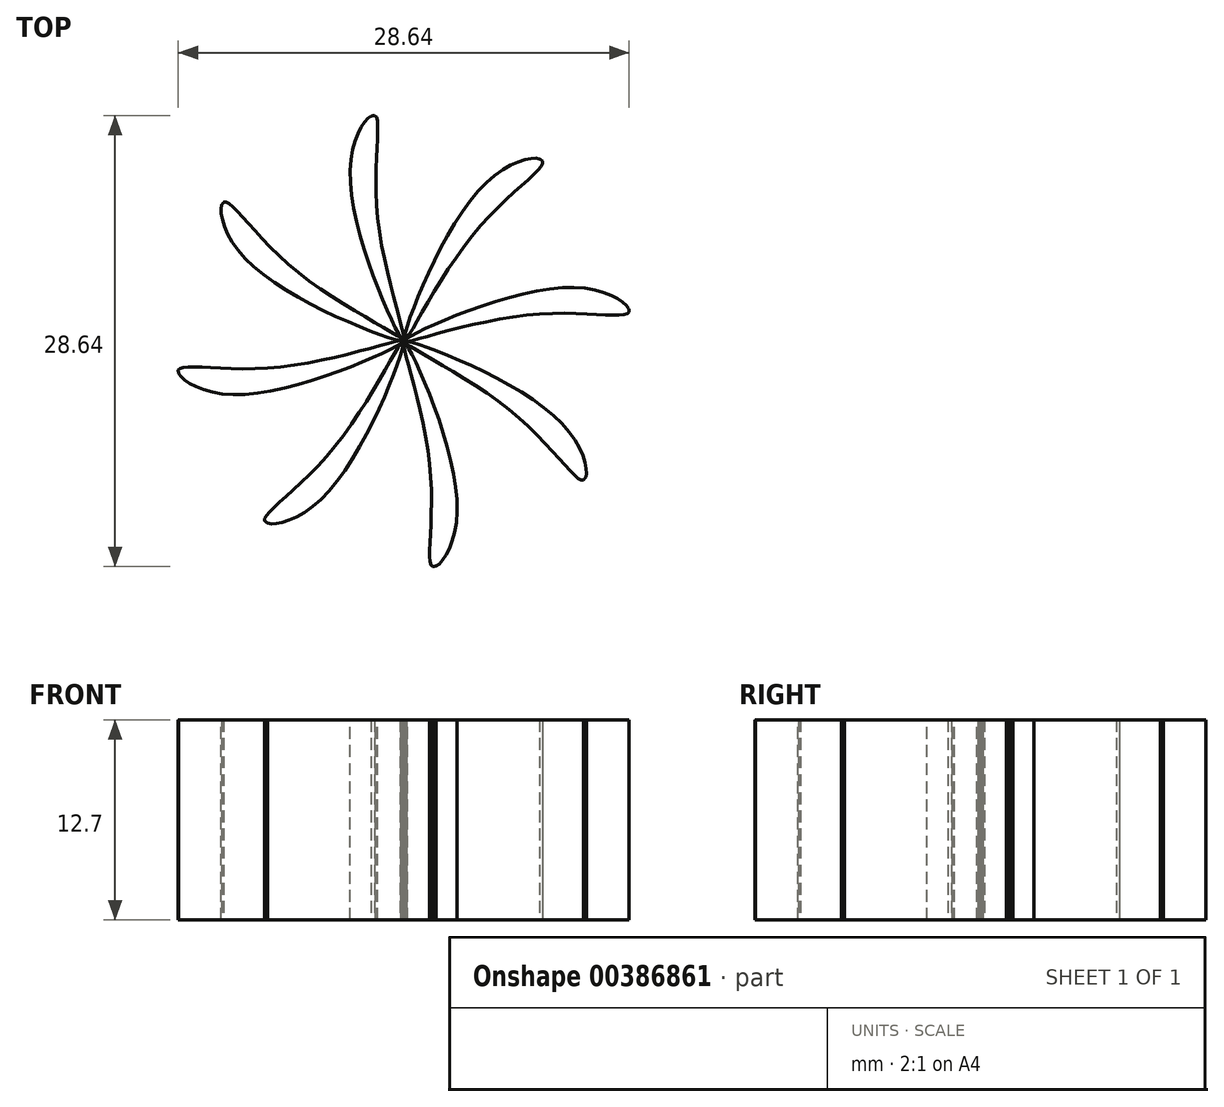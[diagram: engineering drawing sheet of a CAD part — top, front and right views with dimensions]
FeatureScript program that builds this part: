
annotation { "Feature Type Name" : "Feature", "Feature Type Description" : "" }
export const myFeature = defineFeature(function(context is Context, id is Id, definition is map)
    precondition{}
    {
        {
            var Q0;
            Q0=qCreatedBy(makeId("Top.planeOp"),FACE);
            var sketch = newSketch(context, id + "F0", { "sketchPlane" : qUnion([Q0])});
            skCircle(sketch, "E0", {"center": v(0, 0) * mm, "radius": 14.44 * mm});
            skFitSpline(sketch, "E1", {"points": [v(0, 0) * mm, v(-3.4, 10.76) * mm, v(-1.84, 14.32) * mm, v(-1.68, 8.08) * mm, v(0, 0) * mm]});
            skFitSpline(sketch, "E2", {"points": [v(0, 0) * mm, v(5.2, 10.02) * mm, v(8.83, 11.43) * mm, v(4.53, 6.9) * mm, v(0, 0) * mm]});
            skFitSpline(sketch, "E3", {"points": [v(0, 0) * mm, v(10.76, 3.4) * mm, v(14.32, 1.84) * mm, v(8.08, 1.68) * mm, v(0, 0) * mm]});
            skFitSpline(sketch, "E4", {"points": [v(0, 0) * mm, v(10.02, -5.2) * mm, v(11.43, -8.83) * mm, v(6.9, -4.53) * mm, v(0, 0) * mm]});
            skFitSpline(sketch, "E5", {"points": [v(0, 0) * mm, v(-10.02, 5.2) * mm, v(-11.43, 8.83) * mm, v(-6.9, 4.53) * mm, v(0, 0) * mm]});
            skFitSpline(sketch, "E6", {"points": [v(0, 0) * mm, v(-10.76, -3.4) * mm, v(-14.32, -1.84) * mm, v(-8.08, -1.68) * mm, v(0, 0) * mm]});
            skFitSpline(sketch, "E7", {"points": [v(0, 0) * mm, v(-5.2, -10.02) * mm, v(-8.83, -11.43) * mm, v(-4.53, -6.9) * mm, v(0, 0) * mm]});
            skFitSpline(sketch, "E8", {"points": [v(0, 0) * mm, v(3.4, -10.76) * mm, v(1.84, -14.32) * mm, v(1.68, -8.08) * mm, v(0, 0) * mm]});
            skSolve(sketch);
        }
        {
            var Q0;
            {var subQ0=sQuery(id+"F0.wireOp",EDGE,"E5");var subQ1=sQuery(id+"F0.wireOp",EDGE,"E0");var subQ2=makeQuery(id+"F0.imprint","INTERSECT",VERTEX,{"disambiguationData":[OD(0.0)],"derivedFrom":[subQ1,subQ0]});Q0=makeQuery(id+"F0.imprint","IMPRINT",FACE,{"disambiguationData":[TD([[makeQuery(id+"F0.imprint","IMPRINT",EDGE,{"disambiguationData":[TD([[subQ2,-1.0]])],"derivedFrom":subQ1}),1.0]])]});}
            var Q1;
            {var subQ1=sQuery(id+"F0.wireOp",EDGE,"E1");var subQ5=sQuery(id+"F0.wireOp",EDGE,"E0");var subQ6=makeQuery(id+"F0.imprint","INTERSECT",VERTEX,{"disambiguationData":[OD(0.0)],"derivedFrom":[subQ5,subQ1]});Q1=makeQuery(id+"F0.imprint","IMPRINT",FACE,{"disambiguationData":[TD([[makeQuery(id+"F0.imprint","IMPRINT",EDGE,{"disambiguationData":[TD([[subQ6,-1.0]])],"derivedFrom":subQ5}),1.0]])]});}
            var Q2;
            {var subQ0=sQuery(id+"F0.wireOp",EDGE,"E2");var subQ1=sQuery(id+"F0.wireOp",EDGE,"E0");var subQ2=makeQuery(id+"F0.imprint","INTERSECT",VERTEX,{"disambiguationData":[OD(0.0)],"derivedFrom":[subQ1,subQ0]});Q2=makeQuery(id+"F0.imprint","IMPRINT",FACE,{"disambiguationData":[TD([[makeQuery(id+"F0.imprint","IMPRINT",EDGE,{"disambiguationData":[TD([[subQ2,-1.0]])],"derivedFrom":subQ1}),1.0]])]});}
            var Q3;
            {var subQ0=sQuery(id+"F0.wireOp",EDGE,"E3");var subQ1=sQuery(id+"F0.wireOp",EDGE,"E0");var subQ5=makeQuery(id+"F0.imprint","INTERSECT",VERTEX,{"disambiguationData":[OD(0.0)],"derivedFrom":[subQ1,subQ0]});Q3=makeQuery(id+"F0.imprint","IMPRINT",FACE,{"disambiguationData":[TD([[makeQuery(id+"F0.imprint","IMPRINT",EDGE,{"disambiguationData":[TD([[subQ5,1.0]])],"derivedFrom":subQ1}),1.0]])]});}
            var Q4;
            {var subQ0=sQuery(id+"F0.wireOp",EDGE,"E4");var subQ1=sQuery(id+"F0.wireOp",EDGE,"E0");var subQ2=makeQuery(id+"F0.imprint","INTERSECT",VERTEX,{"disambiguationData":[OD(0.0)],"derivedFrom":[subQ1,subQ0]});Q4=makeQuery(id+"F0.imprint","IMPRINT",FACE,{"disambiguationData":[TD([[makeQuery(id+"F0.imprint","IMPRINT",EDGE,{"disambiguationData":[TD([[subQ2,-1.0]])],"derivedFrom":subQ1}),1.0]])]});}
            var Q5;
            {var subQ0=sQuery(id+"F0.wireOp",EDGE,"E8");var subQ5=sQuery(id+"F0.wireOp",EDGE,"E0");var subQ8=makeQuery(id+"F0.imprint","INTERSECT",VERTEX,{"disambiguationData":[OD(0.0)],"derivedFrom":[subQ5,subQ0]});Q5=makeQuery(id+"F0.imprint","IMPRINT",FACE,{"disambiguationData":[TD([[makeQuery(id+"F0.imprint","IMPRINT",EDGE,{"disambiguationData":[TD([[subQ8,-1.0]])],"derivedFrom":subQ5}),1.0]])]});}
            var Q6;
            {var subQ0=sQuery(id+"F0.wireOp",EDGE,"E7");var subQ1=sQuery(id+"F0.wireOp",EDGE,"E0");var subQ8=makeQuery(id+"F0.imprint","INTERSECT",VERTEX,{"disambiguationData":[OD(0.0)],"derivedFrom":[subQ1,subQ0]});Q6=makeQuery(id+"F0.imprint","IMPRINT",FACE,{"disambiguationData":[TD([[makeQuery(id+"F0.imprint","IMPRINT",EDGE,{"disambiguationData":[TD([[subQ8,-1.0]])],"derivedFrom":subQ1}),1.0]])]});}
            var Q7;
            {var subQ0=sQuery(id+"F0.wireOp",EDGE,"E6");var subQ1=sQuery(id+"F0.wireOp",EDGE,"E0");var subQ2=makeQuery(id+"F0.imprint","INTERSECT",VERTEX,{"disambiguationData":[OD(0.0)],"derivedFrom":[subQ1,subQ0]});Q7=makeQuery(id+"F0.imprint","IMPRINT",FACE,{"disambiguationData":[TD([[makeQuery(id+"F0.imprint","IMPRINT",EDGE,{"disambiguationData":[TD([[subQ2,-1.0]])],"derivedFrom":subQ1}),1.0]])]});}
            extrude(context, id + "F1", {"entities" : qUnion([Q0, Q1, Q2, Q3, Q4, Q5, Q6, Q7]), "depth" : 12.7 * mm});
        }
    });
